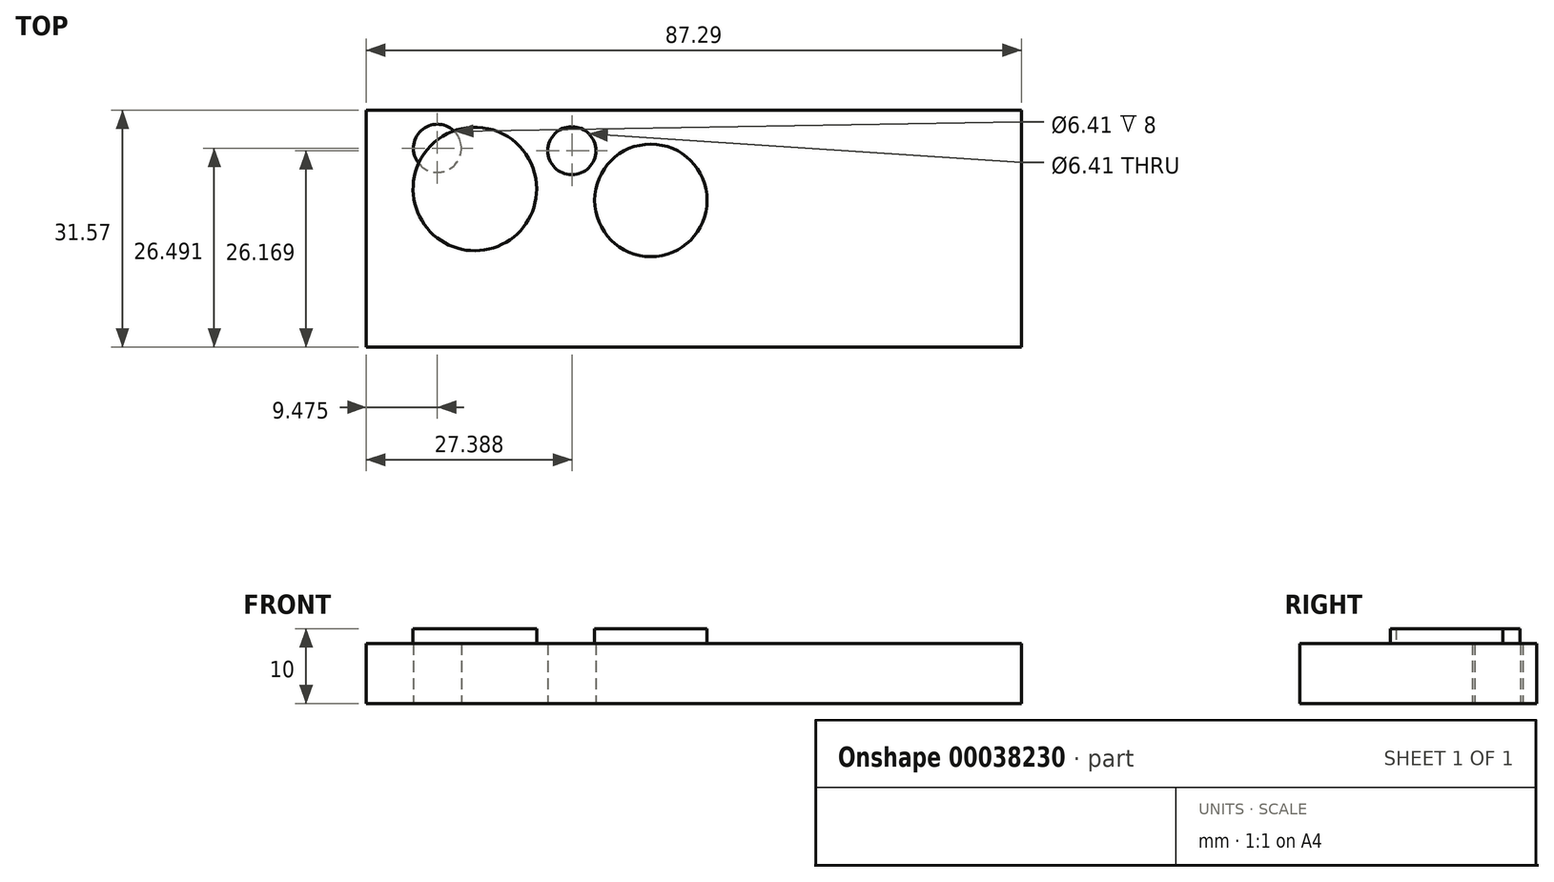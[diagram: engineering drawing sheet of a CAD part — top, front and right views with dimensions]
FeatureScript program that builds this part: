
annotation { "Feature Type Name" : "Feature", "Feature Type Description" : "" }
export const myFeature = defineFeature(function(context is Context, id is Id, definition is map)
    precondition{}
    {
        {
            var Q0;
            Q0=qCreatedBy(makeId("Top.planeOp"),FACE);
            var sketch = newSketch(context, id + "F0", { "sketchPlane" : qUnion([Q0])});
            skLineSegment(sketch, "E0.rect.bottom", {"start": v(20.12, -3.56) * mm, "end": v(-67.17, -3.56) * mm});
            skLineSegment(sketch, "E0.rect.top", {"start": v(20.12, 28.01) * mm, "end": v(-67.17, 28.01) * mm});
            skLineSegment(sketch, "E0.rect.left", {"start": v(20.12, -3.56) * mm, "end": v(20.12, 28.01) * mm});
            skLineSegment(sketch, "E0.rect.right", {"start": v(-67.17, -3.56) * mm, "end": v(-67.17, 28.01) * mm});
            skPoint(sketch, "E0.rect.middle", {"position": v(-23.52, 12.23) * mm});
            skLineSegment(sketch, "E1", {"start": v(-67.17, 28.01) * mm, "end": v(-67.17, 35.03) * mm, "construction": true});
            skLineSegment(sketch, "E2", {"start": v(-67.17, 35.03) * mm, "end": v(20.12, 35.03) * mm, "construction": true});
            skLineSegment(sketch, "E3", {"start": v(20.12, 35.03) * mm, "end": v(20.12, 28.01) * mm, "construction": true});
            skLineSegment(sketch, "E4", {"start": v(20.12, 28.01) * mm, "end": v(27.35, 28.01) * mm});
            skLineSegment(sketch, "E5", {"start": v(27.35, 28.01) * mm, "end": v(27.35, -3.56) * mm, "construction": true});
            skLineSegment(sketch, "E6", {"start": v(27.35, -3.56) * mm, "end": v(20.12, -3.56) * mm});
            skCircle(sketch, "E7", {"center": v(-57.7, 22.93) * mm, "radius": 3.2 * mm});
            skCircle(sketch, "E8", {"center": v(-39.78, 22.6) * mm, "radius": 3.2 * mm});
            skSolve(sketch);
        }
        {
            var Q0;
            Q0=makeQuery(id+"F0.imprint","IMPRINT",FACE,{"disambiguationData":[TD([[makeQuery(id+"F0.imprint","IMPRINT",EDGE,{"derivedFrom":sQuery(id+"F0.wireOp",EDGE,"E0.rect.bottom")}),-1.0]])]});
            extrude(context, id + "F1", {"entities" : qUnion([Q0]), "depth" : 8 * mm});
        }
        {
            var Q0;
            Q0=qCreatedBy(makeId("Top.planeOp"),FACE);
            cPlane(context, id + "F2", {"entities" : qUnion([Q0]), "cplaneType" : CPlaneType.OFFSET, "offset" : 8 * mm, "width" : 150 * mm, "height" : 150 * mm});
        }
        {
            var Q0;
            Q0=qCreatedBy(id+"F2.planeOp",FACE);
            var sketch = newSketch(context, id + "F3", { "sketchPlane" : qUnion([Q0])});
            skCircle(sketch, "E9", {"center": v(-52.7, 17.52) * mm, "radius": 8.23 * mm});
            skCircle(sketch, "E10", {"center": v(-29.25, 16) * mm, "radius": 7.5 * mm});
            skSolve(sketch);
        }
        {
            var Q0;
            Q0=makeQuery(id+"F3.imprint","IMPRINT",FACE,{"disambiguationData":[TD([[makeQuery(id+"F3.imprint","IMPRINT",EDGE,{"derivedFrom":sQuery(id+"F3.wireOp",EDGE,"E9")}),1.0]])]});
            var Q1;
            Q1=makeQuery(id+"F3.imprint","IMPRINT",FACE,{"disambiguationData":[TD([[makeQuery(id+"F3.imprint","IMPRINT",EDGE,{"derivedFrom":sQuery(id+"F3.wireOp",EDGE,"E10")}),1.0]])]});
            extrude(context, id + "F4", {"entities" : qUnion([Q0, Q1]), "operationType" : NewBodyOperationType.ADD, "depth" : 2 * mm});
        }
    });
